# Revit family: Medical-Casework_Shield Casework_Nurse-Server-F2S
name_source: partatom
category: Casework
units: mm (PartAtom-declared; Revit-internal decimal feet)

## family parameters
Always vertical = Yes
Cut with Voids When Loaded = Yes
OmniClass Number = 23.40.35.17.34
OmniClass Title = Medical Casework
Room Calculation Point = No
Shared = No
Work Plane-Based = No

## types (1)
- 30" W x 84" H x 33.5" D
    Assembly Code = E2010200
    Default Elevation = 0 "
    Depth = 33.5 "
    Description = The Nurse Server F2S
    Edition number = 1
    Finish = Acrylic Solid Surface
    Height = 84 "
    Keynote = 12300
    Manufacturer = Shield Casework
    Model = The Nurse Server F2S
    Product Guid = 1f8e4538-9ce1-4ddb-9b3c-7a1fa35f4c92
    Product Material = Shield Casework - Acrylic Solid Surface - S01 White
    Product data url = https://www.bimobject.com
    Product url = https://shieldheadwalls.com
    URL = https://www.shieldcasework.com
    Width = 30 "
    |DoorOpt01 = Door : 00 - Standard Swing Door
    |DoorOpt02 = Door : 02 - Swing Door PPE Storage
    |DoorOpt03 = Door : 03 - Pullout PPE Storage
    |DwOpt01 = Panel : 00 - None
    |DwOpt02 = Panel : 01 - Soap Dispenser
    |DwOpt03 = Panel : 02 - Mask Storage
    |LckOpt01 = Lock : 00 - None
    |LckOpt02 = Lock : 01 - MicroIQ Lock on Patient Room Side
    |LckOpt03 = Lock : 02 - MicroIQ Lock on Corridor Side
    |LckOpt04 = Lock : 03 - MicroIQ Lock on Both Sides
    |PulOpt01 = Pull : 01 - Cut Through
    |PulOpt02 = Pull : 02 - Solid Surface Recessed
    |PulOpt03 = Pull : 03 - Wire Pull
    |PulOpt04 = Pull : 04 - Continuous Tab
    |ShelfOpt01 = Shelves : 01 - One Fixed Shelf
    |ShelfOpt02 = Shelves : 02 - One Fixed Shelf + Two Adjustable Shelves
    |ShelfOpt03 = Shelves : 03 - High Density Storage
    |TopDorHgh = 47.03 "
    |TopDorWdth = 14.95 "
    |TopOpt01 = Top : 01 - Flat Top
    |TopOpt02 = Top : 02 - Sloped Top

## geometry (parser evidence)
native form markers: Sweep x37
no freeform markers — native parametric forms only
